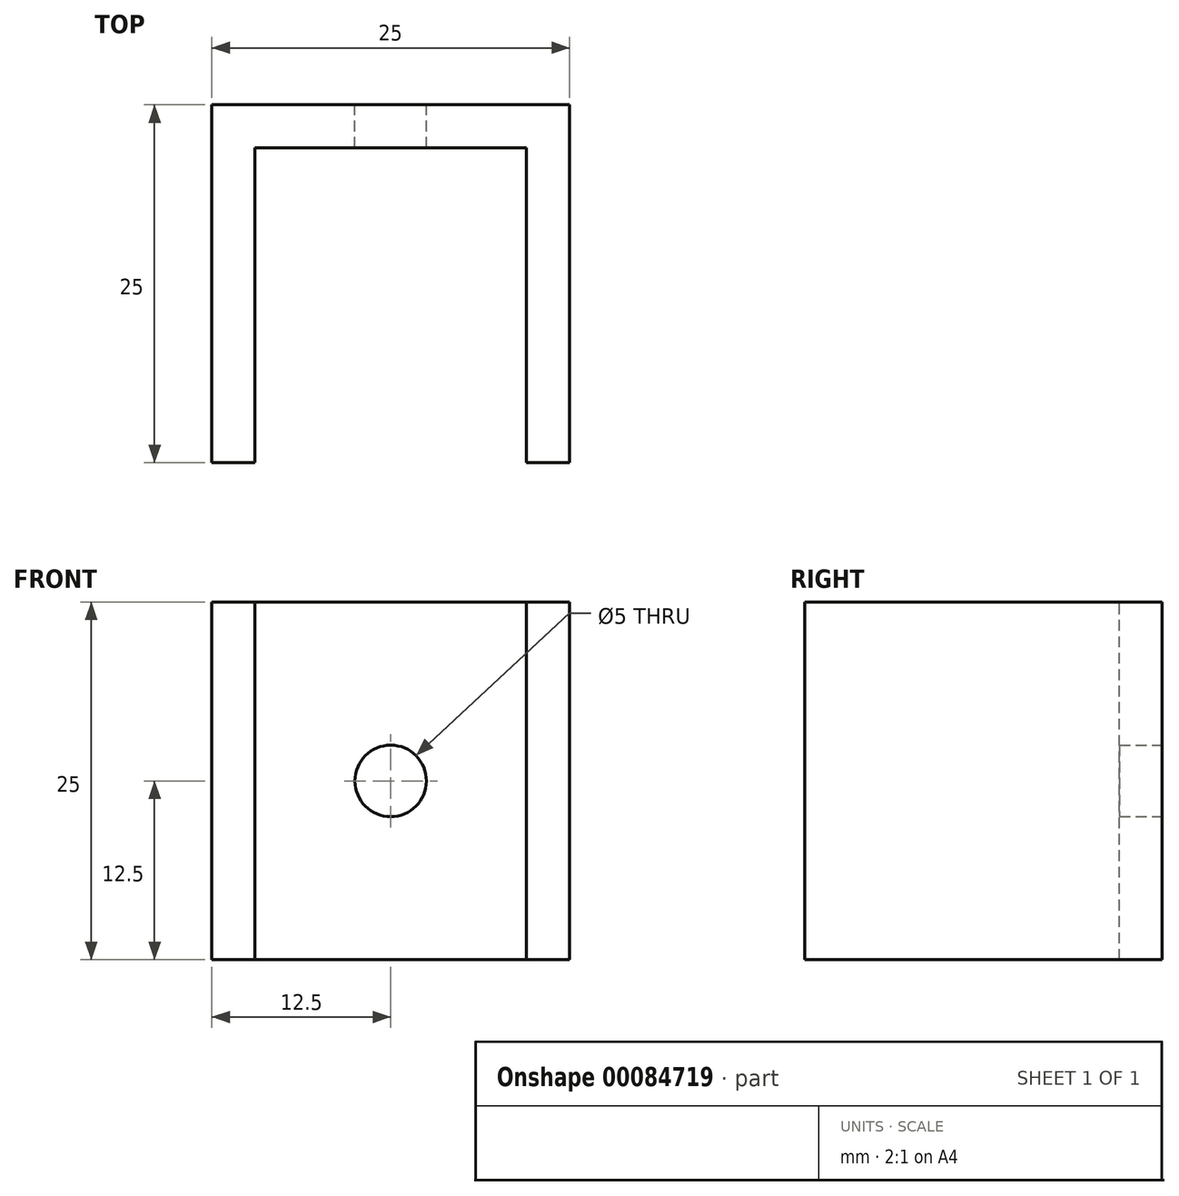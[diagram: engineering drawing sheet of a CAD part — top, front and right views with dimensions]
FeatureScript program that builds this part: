
annotation { "Feature Type Name" : "Feature", "Feature Type Description" : "" }
export const myFeature = defineFeature(function(context is Context, id is Id, definition is map)
    precondition{}
    {
        {
            var Q0;
            Q0=qCreatedBy(makeId("Front.planeOp"),FACE);
            var sketch = newSketch(context, id + "F0", { "sketchPlane" : qUnion([Q0])});
            skLineSegment(sketch, "E0.bottom", {"start": v(-12.5, -12.5) * mm, "end": v(12.5, -12.5) * mm});
            skLineSegment(sketch, "E0.top", {"start": v(-12.5, 12.5) * mm, "end": v(12.5, 12.5) * mm});
            skLineSegment(sketch, "E0.left", {"start": v(-12.5, -12.5) * mm, "end": v(-12.5, 12.5) * mm});
            skLineSegment(sketch, "E0.right", {"start": v(12.5, -12.5) * mm, "end": v(12.5, 12.5) * mm});
            skPoint(sketch, "E0.middle", {"position": v(0, 0) * mm});
            skSolve(sketch);
        }
        {
            var Q0;
            Q0=makeQuery(id+"F0.imprint","IMPRINT",FACE,{"disambiguationData":[TD([[makeQuery(id+"F0.imprint","IMPRINT",EDGE,{"derivedFrom":sQuery(id+"F0.wireOp",EDGE,"E0.bottom")}),1.0]])]});
            extrude(context, id + "F1", {"entities" : qUnion([Q0]), "depth" : 25 * mm});
        }
        {
            var Q0;
            Q0=makeQuery(id+"F1.opExtrude","CAP_FACE",FACE,{"disambiguationData":[OSD([sQuery(id+"F0.wireOp",EDGE,"E0.bottom"),sQuery(id+"F0.wireOp",EDGE,"E0.top"),sQuery(id+"F0.wireOp",EDGE,"E0.left"),sQuery(id+"F0.wireOp",EDGE,"E0.right")])],"isStart":false});
            var Q1;
            Q1=makeQuery(id+"F1.opExtrude","SWEPT_FACE",FACE,{"disambiguationData":[OSD([sQuery(id+"F0.wireOp",EDGE,"E0.bottom")])]});
            var Q2;
            Q2=makeQuery(id+"F1.opExtrude","SWEPT_FACE",FACE,{"disambiguationData":[OSD([sQuery(id+"F0.wireOp",EDGE,"E0.top")])]});
            shell(context, id + "F2", {"entities" : qUnion([Q0, Q1, Q2]), "thickness" : 3 * mm});
        }
        {
            var Q0;
            {var subQ0=sQuery(id+"F0.wireOp",EDGE,"E0.right");var subQ1=sQuery(id+"F0.wireOp",EDGE,"E0.left");var subQ2=sQuery(id+"F0.wireOp",EDGE,"E0.top");var subQ3=sQuery(id+"F0.wireOp",EDGE,"E0.bottom");Q0=makeQuery(id+"F2.opShell","OFFSET_FACE",FACE,{"disambiguationData":[OSD([subQ3,subQ2,subQ1,subQ0]),TDD([makeQuery(id+"F1.opExtrude","CAP_FACE",FACE,{"disambiguationData":[OSD([subQ3,subQ2,subQ1,subQ0])],"isStart":true})])]});}
            var sketch = newSketch(context, id + "F3", { "sketchPlane" : qUnion([Q0])});
            skPoint(sketch, "E1.0", {"position": v(0, 0) * mm});
            skSolve(sketch);
        }
        {
            var Q0;
            Q0=sQuery(id+"F3.wireOp",VERTEX,"E1.0");
            var Q1;
            Q1=makeQuery(id+"F1.opExtrude","SWEPT_BODY",BODY,{"disambiguationData":[OSD([sQuery(id+"F0.wireOp",EDGE,"E0.bottom"),sQuery(id+"F0.wireOp",EDGE,"E0.top"),sQuery(id+"F0.wireOp",EDGE,"E0.left"),sQuery(id+"F0.wireOp",EDGE,"E0.right")])]});
            hole(context, id + "F4", {"style" : HoleStyle.SIMPLE, "endStyle" : HoleEndStyle.BLIND, "standardTappedOrClearance" : lookupTablePath({ "standard" : "ISO", "engagement" : "75%", "pitch" : "1 mm", "size" : "M6", "type" : "Tapped" }), "standardBlindInLast" : lookupTablePath({ "standard" : "ISO", "engagement" : "75%", "pitch" : "1 mm", "size" : "M6", "type" : "Tapped" }), "holeDiameter" : 5 * mm, "holeDepth" : 12 * mm, "startFromSketch" : true, "locations" : qUnion([Q0]), "scope" : qUnion([Q1]), "majorDiameter" : 6 * mm});
        }
    });
